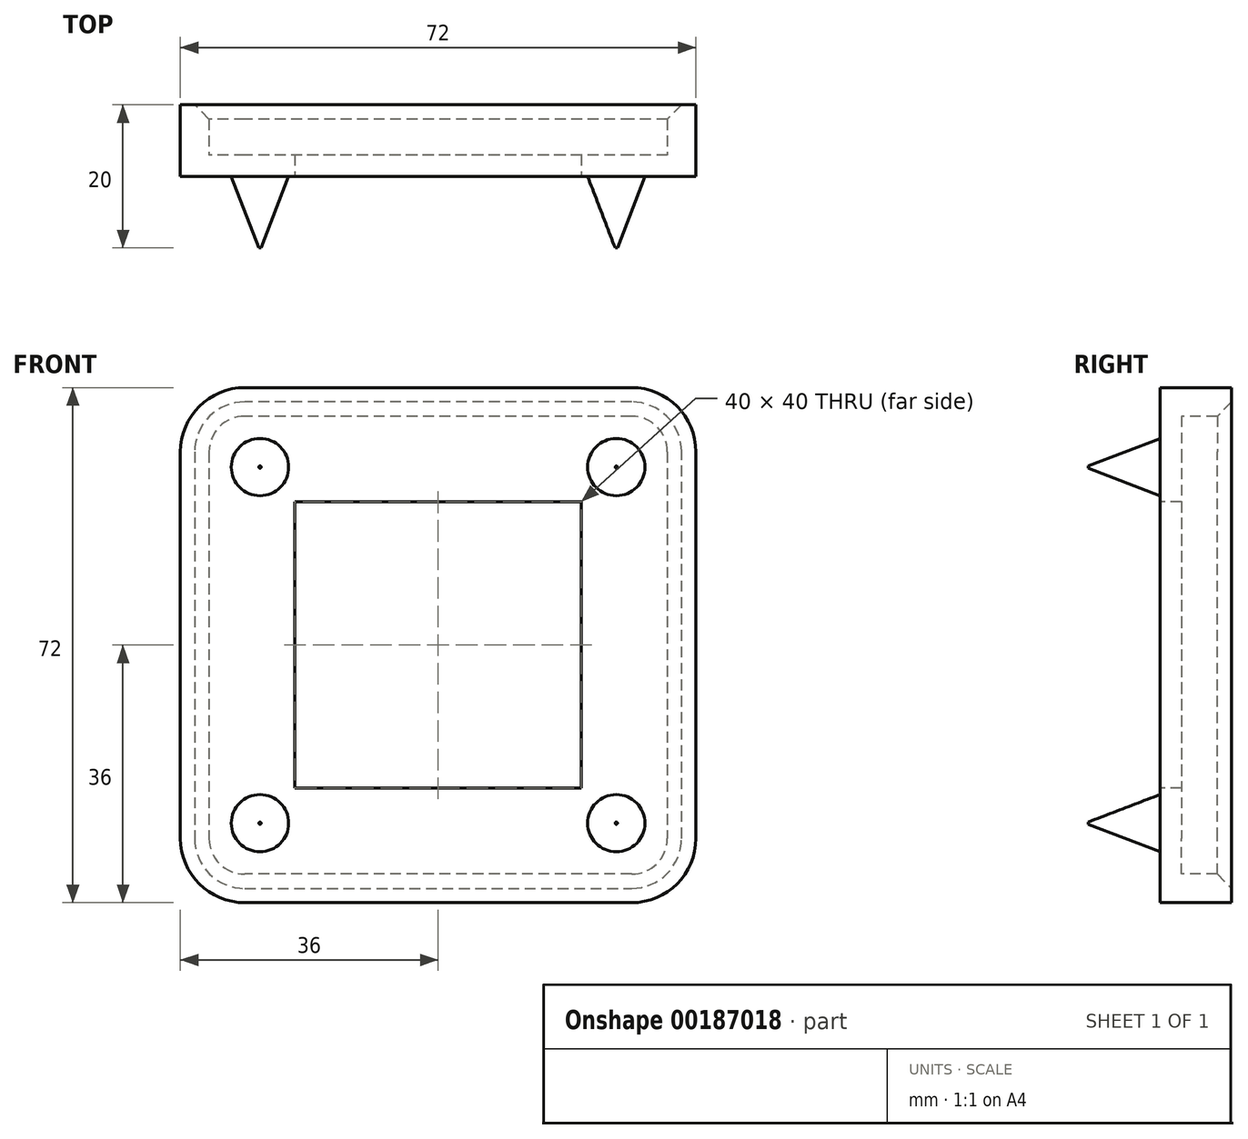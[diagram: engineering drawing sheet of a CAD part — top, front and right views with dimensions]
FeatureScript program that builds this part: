
annotation { "Feature Type Name" : "Feature", "Feature Type Description" : "" }
export const myFeature = defineFeature(function(context is Context, id is Id, definition is map)
    precondition{}
    {
        {
            var Q0;
            Q0=qCreatedBy(makeId("Front.planeOp"),FACE);
            var sketch = newSketch(context, id + "F0", { "sketchPlane" : qUnion([Q0])});
            skLineSegment(sketch, "E0.bottom", {"start": v(27, 32) * mm, "end": v(-27, 32) * mm});
            skLineSegment(sketch, "E0.top", {"start": v(27, -32) * mm, "end": v(-27, -32) * mm});
            skLineSegment(sketch, "E0.left", {"start": v(32, 27) * mm, "end": v(32, -27) * mm});
            skLineSegment(sketch, "E0.right", {"start": v(-32, 27) * mm, "end": v(-32, -27) * mm});
            skPoint(sketch, "E0.middle", {"position": v(0, 0) * mm});
            skPoint(sketch, "E1.visualSharp", {"position": v(-32, 32) * mm});
            skArc(sketch, "E1.filletArc", {"start": v(-27, 32) * mm, "mid": v(-30.54, 30.54) * mm, "end": v(-32, 27) * mm});
            skPoint(sketch, "E2.visualSharp", {"position": v(-32, -32) * mm});
            skArc(sketch, "E2.filletArc", {"start": v(-32, -27) * mm, "mid": v(-30.54, -30.54) * mm, "end": v(-27, -32) * mm});
            skPoint(sketch, "E3.visualSharp", {"position": v(32, -32) * mm});
            skArc(sketch, "E3.filletArc", {"start": v(27, -32) * mm, "mid": v(30.54, -30.54) * mm, "end": v(32, -27) * mm});
            skPoint(sketch, "E4.visualSharp", {"position": v(32, 32) * mm});
            skArc(sketch, "E4.filletArc", {"start": v(32, 27) * mm, "mid": v(30.54, 30.54) * mm, "end": v(27, 32) * mm});
            skArc(sketch, "E5.0", {"start": v(36, 27) * mm, "mid": v(33.36, 33.36) * mm, "end": v(27, 36) * mm});
            skLineSegment(sketch, "E5.1", {"start": v(27, 36) * mm, "end": v(-27, 36) * mm});
            skLineSegment(sketch, "E5.2", {"start": v(36, 27) * mm, "end": v(36, -27) * mm});
            skArc(sketch, "E5.3", {"start": v(-27, 36) * mm, "mid": v(-33.36, 33.36) * mm, "end": v(-36, 27) * mm});
            skArc(sketch, "E5.4", {"start": v(27, -36) * mm, "mid": v(33.36, -33.36) * mm, "end": v(36, -27) * mm});
            skLineSegment(sketch, "E5.5", {"start": v(27, -36) * mm, "end": v(-27, -36) * mm});
            skArc(sketch, "E5.6", {"start": v(-36, -27) * mm, "mid": v(-33.36, -33.36) * mm, "end": v(-27, -36) * mm});
            skLineSegment(sketch, "E5.7", {"start": v(-36, 27) * mm, "end": v(-36, -27) * mm});
            skSolve(sketch);
        }
        {
            var Q0;
            Q0=makeQuery(id+"F0.imprint","IMPRINT",FACE,{"disambiguationData":[TD([[makeQuery(id+"F0.imprint","IMPRINT",EDGE,{"derivedFrom":sQuery(id+"F0.wireOp",EDGE,"E0.bottom")}),1.0]])]});
            extrude(context, id + "F1", {"entities" : qUnion([Q0]), "depth" : 3 * mm});
        }
        {
            var Q0;
            Q0=makeQuery(id+"F1.opExtrude","CAP_FACE",FACE,{"disambiguationData":[OSD([sQuery(id+"F0.wireOp",EDGE,"E0.bottom"),sQuery(id+"F0.wireOp",EDGE,"E0.top"),sQuery(id+"F0.wireOp",EDGE,"E0.left"),sQuery(id+"F0.wireOp",EDGE,"E0.right"),sQuery(id+"F0.wireOp",EDGE,"E1.filletArc"),sQuery(id+"F0.wireOp",EDGE,"E2.filletArc"),sQuery(id+"F0.wireOp",EDGE,"E3.filletArc"),sQuery(id+"F0.wireOp",EDGE,"E4.filletArc")])],"isStart":false});
            var sketch = newSketch(context, id + "F2", { "sketchPlane" : qUnion([Q0])});
            skLineSegment(sketch, "E6", {"start": v(0, 0) * mm, "end": v(-30.54, 30.54) * mm, "construction": true});
            skCircle(sketch, "E7", {"center": v(-24.88, 24.88) * mm, "radius": 4 * mm});
            skSolve(sketch);
        }
        {
            var Q0;
            Q0 = qSketchRegion(id + "F2", true);
            extrude(context, id + "F3", {"entities" : qUnion([Q0]), "depth" : 10 * mm, "hasDraft" : true, "draftAngle" : 21 * degree, "draftPullDirection" : true});
        }
        {
            var Q0;
            Q0=qCreatedBy(makeId("Top.planeOp"),FACE);
            var sketch = newSketch(context, id + "F4", { "sketchPlane" : qUnion([Q0])});
            skLineSegment(sketch, "E8", {"start": v(0, 0) * mm, "end": v(0, -33.23) * mm, "construction": true});
            skSolve(sketch);
        }
        {
            var Q0;
            Q0=makeQuery(id+"F3.opExtrude","SWEPT_BODY",BODY,{"disambiguationData":[OSD([sQuery(id+"F2.wireOp",EDGE,"E7")])]});
            var Q1;
            Q1=sQuery(id+"F4.wireOp",EDGE,"E8");
            circularPattern(context, id + "F5", {"entities" : qUnion([Q0]), "axis" : qUnion([Q1]), "angle" : 90 * degree, "instanceCount" : 4});
        }
        {
            var Q0;
            Q0=makeQuery(id+"F1.opExtrude","CAP_FACE",FACE,{"disambiguationData":[OSD([sQuery(id+"F0.wireOp",EDGE,"E0.bottom"),sQuery(id+"F0.wireOp",EDGE,"E0.top"),sQuery(id+"F0.wireOp",EDGE,"E0.left"),sQuery(id+"F0.wireOp",EDGE,"E0.right"),sQuery(id+"F0.wireOp",EDGE,"E1.filletArc"),sQuery(id+"F0.wireOp",EDGE,"E2.filletArc"),sQuery(id+"F0.wireOp",EDGE,"E3.filletArc"),sQuery(id+"F0.wireOp",EDGE,"E4.filletArc")])],"isStart":false});
            var sketch = newSketch(context, id + "F6", { "sketchPlane" : qUnion([Q0])});
            skLineSegment(sketch, "E9.0", {"start": v(-36, 27) * mm, "end": v(-36, -27) * mm});
            skArc(sketch, "E10.0", {"start": v(-36, -27) * mm, "mid": v(-33.36, -33.36) * mm, "end": v(-27, -36) * mm});
            skLineSegment(sketch, "E11.0.0", {"start": v(36, -27) * mm, "end": v(36, 27) * mm});
            skArc(sketch, "E11.0.1", {"start": v(36, 27) * mm, "mid": v(33.36, 33.36) * mm, "end": v(27, 36) * mm});
            skLineSegment(sketch, "E11.0.2", {"start": v(27, 36) * mm, "end": v(-27, 36) * mm});
            skArc(sketch, "E11.0.3", {"start": v(-27, 36) * mm, "mid": v(-33.36, 33.36) * mm, "end": v(-36, 27) * mm});
            skLineSegment(sketch, "E11.0.6", {"start": v(-27, -36) * mm, "end": v(27, -36) * mm});
            skArc(sketch, "E11.0.7", {"start": v(27, -36) * mm, "mid": v(33.36, -33.36) * mm, "end": v(36, -27) * mm});
            skSolve(sketch);
        }
        {
            var Q0;
            Q0=makeQuery(id+"F6.imprint","IMPRINT",FACE,{"disambiguationData":[TD([[makeQuery(id+"F6.imprint","IMPRINT",EDGE,{"derivedFrom":sQuery(id+"F6.wireOp",EDGE,"E11.0.0")}),1.0]])]});
            extrude(context, id + "F7", {"entities" : qUnion([Q0]), "operationType" : NewBodyOperationType.ADD, "oppositeDirection" : true, "depth" : 10 * mm});
        }
        {
            var Q0;
            Q0=makeQuery(id+"F6.imprint","IMPRINT",FACE,{"disambiguationData":[TD([[makeQuery(id+"F6.imprint","IMPRINT",EDGE,{"derivedFrom":makeQuery(id+"F1.opExtrude","CAP_EDGE",EDGE,{"disambiguationData":[OSD([sQuery(id+"F0.wireOp",EDGE,"E0.bottom")])],"isStart":false})}),1.0]])]});
            var sketch = newSketch(context, id + "F8", { "sketchPlane" : qUnion([Q0])});
            skLineSegment(sketch, "E12.bottom", {"start": v(20, 20) * mm, "end": v(-20, 20) * mm});
            skLineSegment(sketch, "E12.top", {"start": v(20, -20) * mm, "end": v(-20, -20) * mm});
            skLineSegment(sketch, "E12.left", {"start": v(20, 20) * mm, "end": v(20, -20) * mm});
            skLineSegment(sketch, "E12.right", {"start": v(-20, 20) * mm, "end": v(-20, -20) * mm});
            skPoint(sketch, "E12.middle", {"position": v(0, 0) * mm});
            skSolve(sketch);
        }
        {
            var Q0;
            Q0=makeQuery(id+"F8.imprint","IMPRINT",FACE,{"disambiguationData":[TD([[makeQuery(id+"F8.imprint","IMPRINT",EDGE,{"derivedFrom":sQuery(id+"F8.wireOp",EDGE,"E12.bottom")}),1.0]])]});
            extrude(context, id + "F9", {"entities" : qUnion([Q0]), "operationType" : NewBodyOperationType.REMOVE, "oppositeDirection" : true, "depth" : 3 * mm});
        }
        {
            var Q0;
            Q0=makeQuery(id+"F7.opExtrude","CAP_EDGE",EDGE,{"disambiguationData":[OSD([sQuery(id+"F0.wireOp",EDGE,"E0.top")])],"isStart":false});
            var Q1;
            Q1=makeQuery(id+"F9.boolean.opBoolean","COPY",EDGE,{"derivedFrom":makeQuery(id+"F9.opExtrude","CAP_EDGE",EDGE,{"disambiguationData":[OSD([sQuery(id+"F8.wireOp",EDGE,"E12.top")])],"isStart":false})});
            var Q2;
            Q2=makeQuery(id+"F9.boolean.opBoolean","COPY",EDGE,{"derivedFrom":makeQuery(id+"F9.opExtrude","CAP_EDGE",EDGE,{"disambiguationData":[OSD([sQuery(id+"F8.wireOp",EDGE,"E12.left")])],"isStart":false})});
            var Q3;
            Q3=makeQuery(id+"F9.boolean.opBoolean","COPY",EDGE,{"derivedFrom":makeQuery(id+"F9.opExtrude","CAP_EDGE",EDGE,{"disambiguationData":[OSD([sQuery(id+"F8.wireOp",EDGE,"E12.right")])],"isStart":false})});
            var Q4;
            Q4=makeQuery(id+"F9.boolean.opBoolean","COPY",EDGE,{"derivedFrom":makeQuery(id+"F9.opExtrude","CAP_EDGE",EDGE,{"disambiguationData":[OSD([sQuery(id+"F8.wireOp",EDGE,"E12.bottom")])],"isStart":false})});
            chamfer(context, id + "F10", {"entities" : qUnion([Q0, Q1, Q2, Q3, Q4]), "width" : 2 * mm, "tangentPropagation" : true});
        }
    });
